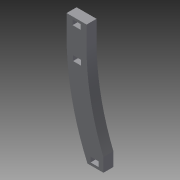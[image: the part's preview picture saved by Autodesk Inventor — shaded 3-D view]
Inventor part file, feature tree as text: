
AUTODESK INVENTOR PART (.ipt)
format: ipt  version: 2013 (Build 170138000, 138)  size: 147,456 bytes
history: native  units: in
note: dims shown in document units (in); Inventor stores cm internally (conversion verified against a paired STEP export)
features: extrude x7, sketch x6
ambient origin geometry x8: Origin, YZ Plane, XZ Plane, XY Plane, X Axis, Y Axis, Z Axis, Center Point
bodies: Solid1 (feature_tree)
feature tree (13):
  extrude  "Extrusion1"  Depth=1.0in
  extrude  "Extrusion2"  Depth=5.0in
  extrude  "Extrusion3"  Depth=1.0in TaperAngle=0.0deg
  extrude  "Extrusion4"  Depth=0.25in
  extrude  "Extrusion5"  Depth=0.1936in
  extrude  "Extrusion6"  Depth=1.0in
  extrude  "Extrusion8"  Depth=0.5in TaperAngle=0.0deg
  sketch  "Sketch1"  dims[d0=23.0in d1=1.0in]
  sketch  "Sketch2"  dims[d2=1.0in d3=5.0in]
  sketch  "Sketch4"  dims[d4=0.5in d5=0.0in d6=1.0in d7=0.0in]
  sketch  "Sketch5"  dims[d16=0.2in d17=0.25in]
  sketch  "Sketch6"  dims[d18=0.4in d20=0.1936in]
  sketch  "Sketch7"  dims[d22=1.0in d23=0.0in d24=1.0in d25=0.5in d26=0.0in d27=0.125in d28=0.2in d29=0.25in d30=0.4in d31=10.0in d32=0.0in d33=0.55in d34=0.375in d35=0.35in d36=0.8in d37=0.5438in d38=10.0in d39=0.0in d59=0.323in d60=0.25in d61=0.4in d63=1.0in d64=0.0in d65=1.668in]
